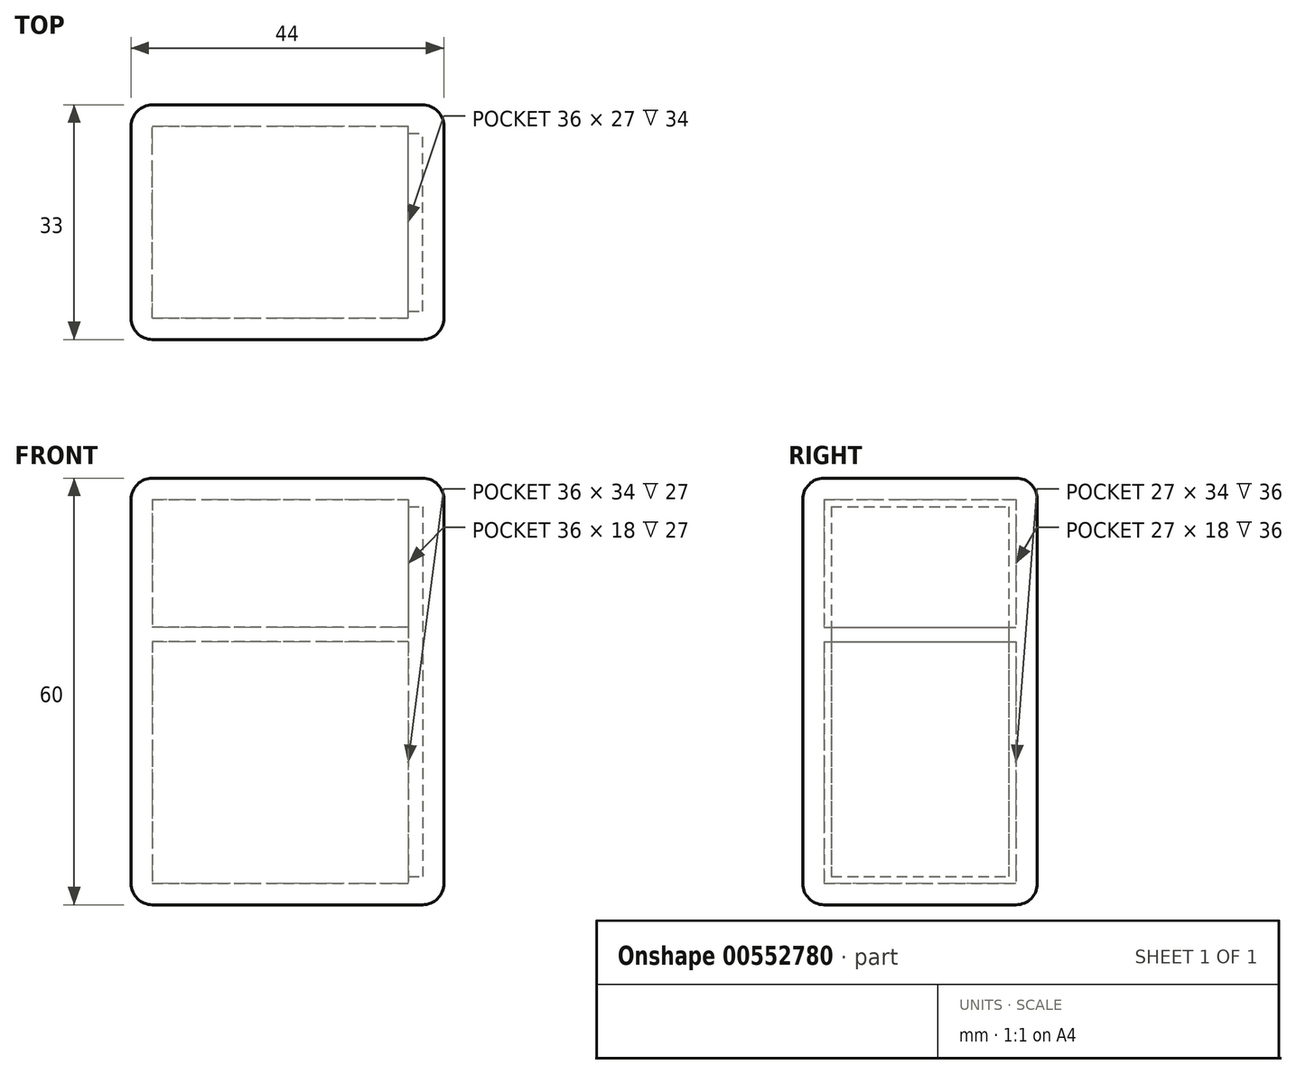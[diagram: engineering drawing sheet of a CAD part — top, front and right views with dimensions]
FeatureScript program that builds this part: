
annotation { "Feature Type Name" : "Feature", "Feature Type Description" : "" }
export const myFeature = defineFeature(function(context is Context, id is Id, definition is map)
    precondition{}
    {
        {
            var Q0;
            Q0=qCreatedBy(makeId("Top.planeOp"),FACE);
            var sketch = newSketch(context, id + "F0", { "sketchPlane" : qUnion([Q0])});
            skLineSegment(sketch, "E0.bottom", {"start": v(0, 0) * mm, "end": v(41, 0) * mm});
            skLineSegment(sketch, "E0.top", {"start": v(0, -33) * mm, "end": v(41, -33) * mm});
            skLineSegment(sketch, "E0.left", {"start": v(0, 0) * mm, "end": v(0, -33) * mm});
            skLineSegment(sketch, "E0.right", {"start": v(41, 0) * mm, "end": v(41, -33) * mm});
            skSolve(sketch);
        }
        {
            var Q0;
            Q0=makeQuery(id+"F0.imprint","IMPRINT",FACE,{"disambiguationData":[TD([[makeQuery(id+"F0.imprint","IMPRINT",EDGE,{"derivedFrom":sQuery(id+"F0.wireOp",EDGE,"E0.bottom")}),-1.0]])]});
            extrude(context, id + "F1", {"entities" : qUnion([Q0]), "depth" : 60 * mm, "offsetDistance" : 25 * mm});
        }
        {
            var Q0;
            Q0=makeQuery(id+"F1.opExtrude","SWEPT_FACE",FACE,{"disambiguationData":[OSD([sQuery(id+"F0.wireOp",EDGE,"E0.right")])]});
            shell(context, id + "F2", {"entities" : qUnion([Q0]), "thickness" : 3 * mm});
        }
        {
            var Q0;
            Q0=makeQuery(id+"F2.opShell","OFFSET_FACE",FACE,{"disambiguationData":[OSD([sQuery(id+"F0.wireOp",EDGE,"E0.left")])]});
            var sketch = newSketch(context, id + "F3", { "sketchPlane" : qUnion([Q0])});
            skLineSegment(sketch, "E1.bottom", {"start": v(-30, 37) * mm, "end": v(-3, 37) * mm});
            skLineSegment(sketch, "E1.top", {"start": v(-30, 39) * mm, "end": v(-3, 39) * mm});
            skLineSegment(sketch, "E1.left", {"start": v(-30, 37) * mm, "end": v(-30, 39) * mm});
            skLineSegment(sketch, "E1.right", {"start": v(-3, 37) * mm, "end": v(-3, 39) * mm});
            skSolve(sketch);
        }
        {
            var Q0;
            Q0 = qSketchRegion(id + "F3", true);
            extrude(context, id + "F4", {"entities" : qUnion([Q0]), "operationType" : NewBodyOperationType.ADD, "depth" : 36 * mm, "offsetDistance" : 25 * mm});
        }
        {
            var Q0;
            Q0=makeQuery(id+"F4.boolean.opBoolean","MERGE",FACE,{"derivedFrom":[makeQuery(id+"F1.opExtrude","SWEPT_FACE",FACE,{"disambiguationData":[OSD([sQuery(id+"F0.wireOp",EDGE,"E0.right")])]}),makeQuery(id+"F4.opExtrude","CAP_FACE",FACE,{"disambiguationData":[OSD([sQuery(id+"F3.wireOp",EDGE,"E1.bottom"),sQuery(id+"F3.wireOp",EDGE,"E1.top"),sQuery(id+"F3.wireOp",EDGE,"E1.left"),sQuery(id+"F3.wireOp",EDGE,"E1.right")])],"isStart":false})]});
            var sketch = newSketch(context, id + "F5", { "sketchPlane" : qUnion([Q0])});
            skLineSegment(sketch, "E2.bottom", {"start": v(0, 60) * mm, "end": v(-33, 60) * mm});
            skLineSegment(sketch, "E2.top", {"start": v(0, 0) * mm, "end": v(-33, 0) * mm});
            skLineSegment(sketch, "E2.left", {"start": v(0, 60) * mm, "end": v(0, 0) * mm});
            skLineSegment(sketch, "E2.right", {"start": v(-33, 60) * mm, "end": v(-33, 0) * mm});
            skSolve(sketch);
        }
        {
            var Q0;
            Q0 = qSketchRegion(id + "F5", true);
            extrude(context, id + "F6", {"entities" : qUnion([Q0]), "depth" : 3 * mm, "offsetDistance" : 25 * mm});
        }
        {
            var Q0;
            Q0=makeQuery(id+"F6.opExtrude","CAP_FACE",FACE,{"disambiguationData":[OSD([sQuery(id+"F5.wireOp",EDGE,"E2.bottom"),sQuery(id+"F5.wireOp",EDGE,"E2.top"),sQuery(id+"F5.wireOp",EDGE,"E2.left"),sQuery(id+"F5.wireOp",EDGE,"E2.right")])],"isStart":true});
            var sketch = newSketch(context, id + "F7", { "sketchPlane" : qUnion([Q0])});
            skLineSegment(sketch, "E3.bottom", {"start": v(30, 57) * mm, "end": v(3, 57) * mm});
            skLineSegment(sketch, "E3.top", {"start": v(30, 3) * mm, "end": v(3, 3) * mm});
            skLineSegment(sketch, "E3.left", {"start": v(30, 57) * mm, "end": v(30, 3) * mm});
            skLineSegment(sketch, "E3.right", {"start": v(3, 57) * mm, "end": v(3, 3) * mm});
            skLineSegment(sketch, "E4.0", {"start": v(29, 56) * mm, "end": v(4, 56) * mm});
            skLineSegment(sketch, "E4.1", {"start": v(29, 56) * mm, "end": v(29, 4) * mm});
            skLineSegment(sketch, "E4.2", {"start": v(29, 4) * mm, "end": v(4, 4) * mm});
            skLineSegment(sketch, "E4.3", {"start": v(4, 56) * mm, "end": v(4, 4) * mm});
            skSolve(sketch);
        }
        {
            var Q0;
            Q0 = qSketchRegion(id + "F7", true);
            extrude(context, id + "F8", {"entities" : qUnion([Q0]), "operationType" : NewBodyOperationType.ADD, "depth" : 2 * mm, "offsetDistance" : 25 * mm});
        }
        {
            var Q0;
            Q0=makeQuery(id+"F1.opExtrude","CAP_EDGE",EDGE,{"disambiguationData":[OSD([sQuery(id+"F0.wireOp",EDGE,"E0.top")])],"isStart":false});
            var Q1;
            Q1=makeQuery(id+"F1.opExtrude","CAP_EDGE",EDGE,{"disambiguationData":[OSD([sQuery(id+"F0.wireOp",EDGE,"E0.bottom")])],"isStart":false});
            var Q2;
            Q2=makeQuery(id+"F1.opExtrude","CAP_EDGE",EDGE,{"disambiguationData":[OSD([sQuery(id+"F0.wireOp",EDGE,"E0.bottom")])],"isStart":true});
            var Q3;
            Q3=makeQuery(id+"F1.opExtrude","CAP_EDGE",EDGE,{"disambiguationData":[OSD([sQuery(id+"F0.wireOp",EDGE,"E0.top")])],"isStart":true});
            var Q4;
            Q4=makeQuery(id+"F1.opExtrude","SWEPT_EDGE",EDGE,{"disambiguationData":[OSD([sQuery(id+"F0.wireOp",EDGE,"E0.top"),sQuery(id+"F0.wireOp",EDGE,"E0.left")])]});
            var Q5;
            Q5=makeQuery(id+"F1.opExtrude","CAP_EDGE",EDGE,{"disambiguationData":[OSD([sQuery(id+"F0.wireOp",EDGE,"E0.left")])],"isStart":false});
            var Q6;
            Q6=makeQuery(id+"F1.opExtrude","SWEPT_EDGE",EDGE,{"disambiguationData":[OSD([sQuery(id+"F0.wireOp",EDGE,"E0.bottom"),sQuery(id+"F0.wireOp",EDGE,"E0.left")])]});
            var Q7;
            Q7=makeQuery(id+"F1.opExtrude","CAP_EDGE",EDGE,{"disambiguationData":[OSD([sQuery(id+"F0.wireOp",EDGE,"E0.left")])],"isStart":true});
            fillet(context, id + "F9", {"entities" : qUnion([Q0, Q1, Q2, Q3, Q4, Q5, Q6, Q7]), "radius" : 3 * mm, "tangentPropagation" : true, "allowEdgeOverflow" : false});
        }
        {
            var Q0;
            Q0=makeQuery(id+"F6.opExtrude","SWEPT_EDGE",EDGE,{"disambiguationData":[OSD([sQuery(id+"F5.wireOp",EDGE,"E2.bottom"),sQuery(id+"F5.wireOp",EDGE,"E2.right")])]});
            var Q1;
            Q1=makeQuery(id+"F6.opExtrude","CAP_EDGE",EDGE,{"disambiguationData":[OSD([sQuery(id+"F5.wireOp",EDGE,"E2.bottom")])],"isStart":false});
            var Q2;
            Q2=makeQuery(id+"F6.opExtrude","CAP_EDGE",EDGE,{"disambiguationData":[OSD([sQuery(id+"F5.wireOp",EDGE,"E2.right")])],"isStart":false});
            var Q3;
            Q3=makeQuery(id+"F6.opExtrude","CAP_EDGE",EDGE,{"disambiguationData":[OSD([sQuery(id+"F5.wireOp",EDGE,"E2.top")])],"isStart":false});
            var Q4;
            Q4=makeQuery(id+"F6.opExtrude","SWEPT_EDGE",EDGE,{"disambiguationData":[OSD([sQuery(id+"F5.wireOp",EDGE,"E2.top"),sQuery(id+"F5.wireOp",EDGE,"E2.right")])]});
            var Q5;
            Q5=makeQuery(id+"F6.opExtrude","SWEPT_EDGE",EDGE,{"disambiguationData":[OSD([sQuery(id+"F5.wireOp",EDGE,"E2.top"),sQuery(id+"F5.wireOp",EDGE,"E2.left")])]});
            var Q6;
            Q6=makeQuery(id+"F6.opExtrude","CAP_EDGE",EDGE,{"disambiguationData":[OSD([sQuery(id+"F5.wireOp",EDGE,"E2.left")])],"isStart":false});
            var Q7;
            Q7=makeQuery(id+"F6.opExtrude","SWEPT_EDGE",EDGE,{"disambiguationData":[OSD([sQuery(id+"F5.wireOp",EDGE,"E2.bottom"),sQuery(id+"F5.wireOp",EDGE,"E2.left")])]});
            fillet(context, id + "F10", {"entities" : qUnion([Q0, Q1, Q2, Q3, Q4, Q5, Q6, Q7]), "radius" : 3 * mm, "tangentPropagation" : true, "allowEdgeOverflow" : false});
        }
    });
